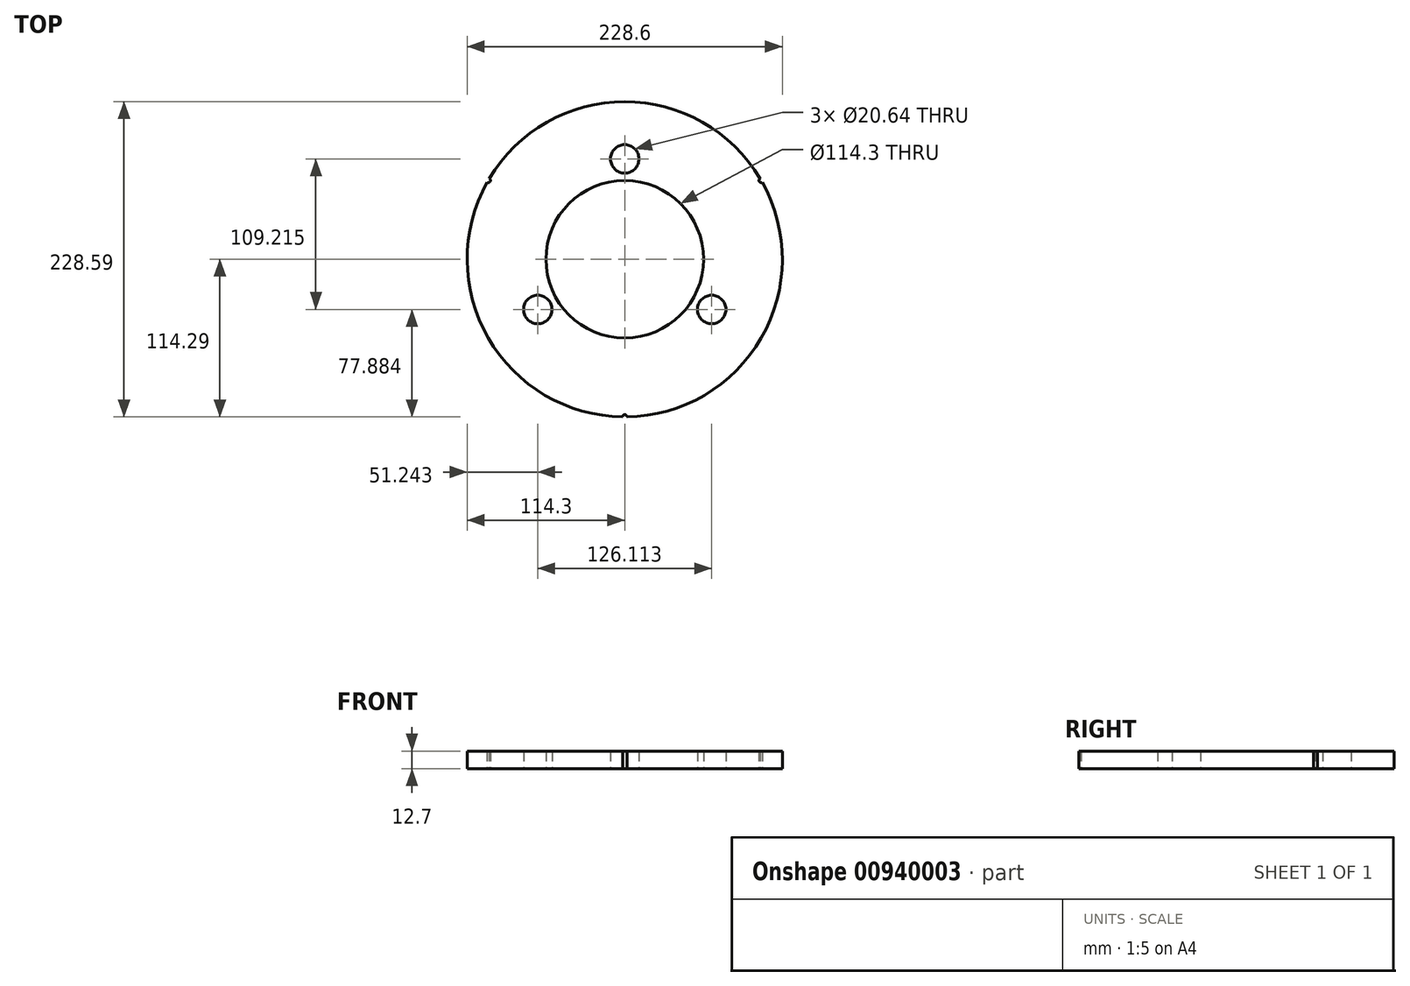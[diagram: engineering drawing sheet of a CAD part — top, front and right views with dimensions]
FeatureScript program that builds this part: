
annotation { "Feature Type Name" : "Feature", "Feature Type Description" : "" }
export const myFeature = defineFeature(function(context is Context, id is Id, definition is map)
    precondition{}
    {
        {
            var Q0;
            Q0=qCreatedBy(makeId("Top.planeOp"),FACE);
            var sketch = newSketch(context, id + "F0", { "sketchPlane" : qUnion([Q0])});
            skCircle(sketch, "E0", {"center": v(0, 0) * mm, "radius": 114.3 * mm});
            skCircle(sketch, "E1", {"center": v(0, 0) * mm, "radius": 57.15 * mm});
            skCircle(sketch, "E2", {"center": v(0, 72.8) * mm, "radius": 10.32 * mm});
            skLineSegment(sketch, "E3", {"start": v(0, 0) * mm, "end": v(63.43, -36.62) * mm, "construction": true});
            skLineSegment(sketch, "E4", {"start": v(0, 0) * mm, "end": v(-75.53, -43.6) * mm, "construction": true});
            skLineSegment(sketch, "E5", {"start": v(0, 0) * mm, "end": v(0, 105.28) * mm, "construction": true});
            skCircle(sketch, "E6", {"center": v(63.06, -36.4) * mm, "radius": 10.32 * mm});
            skCircle(sketch, "E7", {"center": v(-63.06, -36.4) * mm, "radius": 10.32 * mm});
            skLineSegment(sketch, "E8", {"start": v(0, 0) * mm, "end": v(108.11, 62.42) * mm, "construction": true});
            skLineSegment(sketch, "E9", {"start": v(0, 0) * mm, "end": v(-108.61, 62.7) * mm, "construction": true});
            skLineSegment(sketch, "E10", {"start": v(0, 0) * mm, "end": v(0, -139.04) * mm, "construction": true});
            skCircle(sketch, "E11", {"center": v(0, -114.3) * mm, "radius": 1.59 * mm});
            skCircle(sketch, "E12", {"center": v(98.99, 57.15) * mm, "radius": 1.59 * mm});
            skCircle(sketch, "E13", {"center": v(-98.99, 57.15) * mm, "radius": 1.59 * mm});
            skSolve(sketch);
        }
        {
            var Q0;
            Q0=makeQuery(id+"F0.imprint","IMPRINT",FACE,{"disambiguationData":[TD([[makeQuery(id+"F0.imprint","IMPRINT",EDGE,{"derivedFrom":sQuery(id+"F0.wireOp",EDGE,"E2")}),-1.0]])]});
            var Q1;
            Q1=makeQuery(id+"F0.imprint","IMPRINT",FACE,{"disambiguationData":[TD([[makeQuery(id+"F0.imprint","IMPRINT",EDGE,{"derivedFrom":sQuery(id+"F0.wireOp",EDGE,"E7")}),-1.0]])]});
            var Q2;
            Q2=makeQuery(id+"F0.imprint","IMPRINT",FACE,{"disambiguationData":[TD([[makeQuery(id+"F0.imprint","IMPRINT",EDGE,{"derivedFrom":sQuery(id+"F0.wireOp",EDGE,"E6")}),-1.0]])]});
            extrude(context, id + "F1", {"entities" : qUnion([Q0, Q1, Q2]), "depth" : 12.7 * mm, "offsetDistance" : 25.4 * mm});
        }
    });
